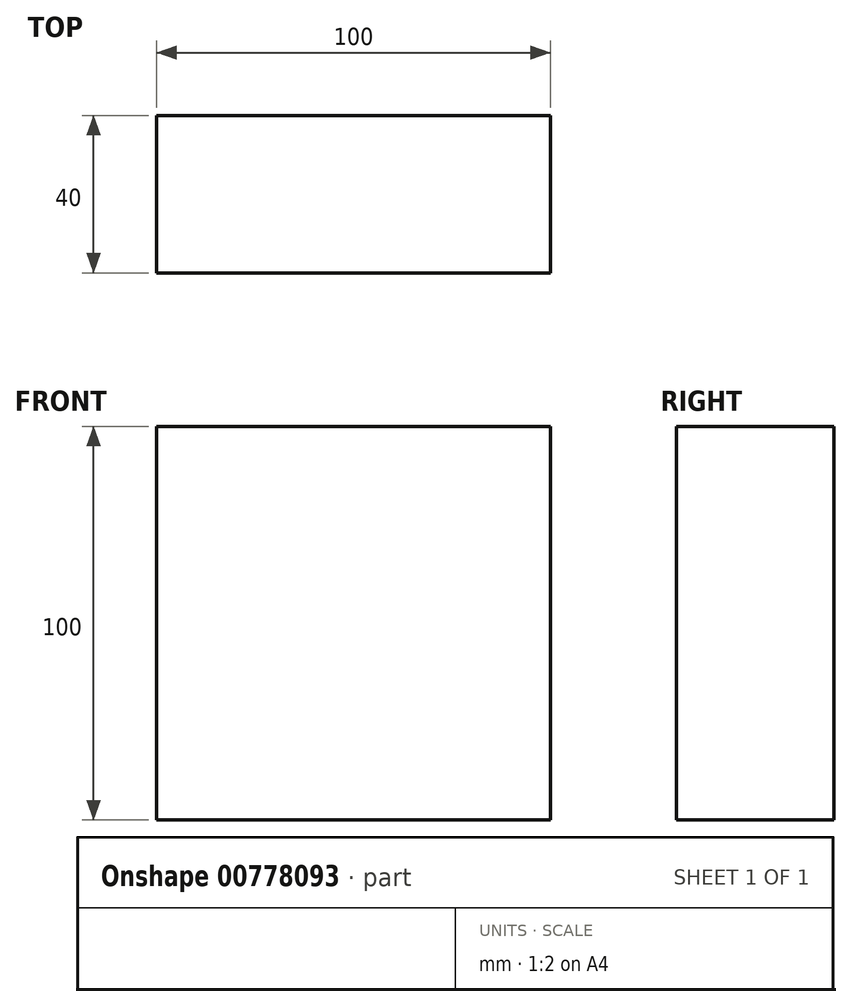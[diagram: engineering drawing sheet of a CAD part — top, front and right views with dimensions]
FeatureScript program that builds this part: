
annotation { "Feature Type Name" : "Feature", "Feature Type Description" : "" }
export const myFeature = defineFeature(function(context is Context, id is Id, definition is map)
    precondition{}
    {
        {
            var Q0;
            Q0=qCreatedBy(makeId("Top.planeOp"),FACE);
            var sketch = newSketch(context, id + "F0", { "sketchPlane" : qUnion([Q0])});
            skLineSegment(sketch, "E0.bottom", {"start": v(0, 0) * mm, "end": v(100, 0) * mm});
            skLineSegment(sketch, "E0.top", {"start": v(0, 40) * mm, "end": v(100, 40) * mm});
            skLineSegment(sketch, "E0.left", {"start": v(0, 0) * mm, "end": v(0, 40) * mm});
            skLineSegment(sketch, "E0.right", {"start": v(100, 0) * mm, "end": v(100, 40) * mm});
            skSolve(sketch);
        }
        {
            var Q0;
            Q0 = qSketchRegion(id + "F0", true);
            extrude(context, id + "F1", {"entities" : qUnion([Q0]), "depth" : 100 * mm, "offsetDistance" : 25 * mm});
        }
    });
